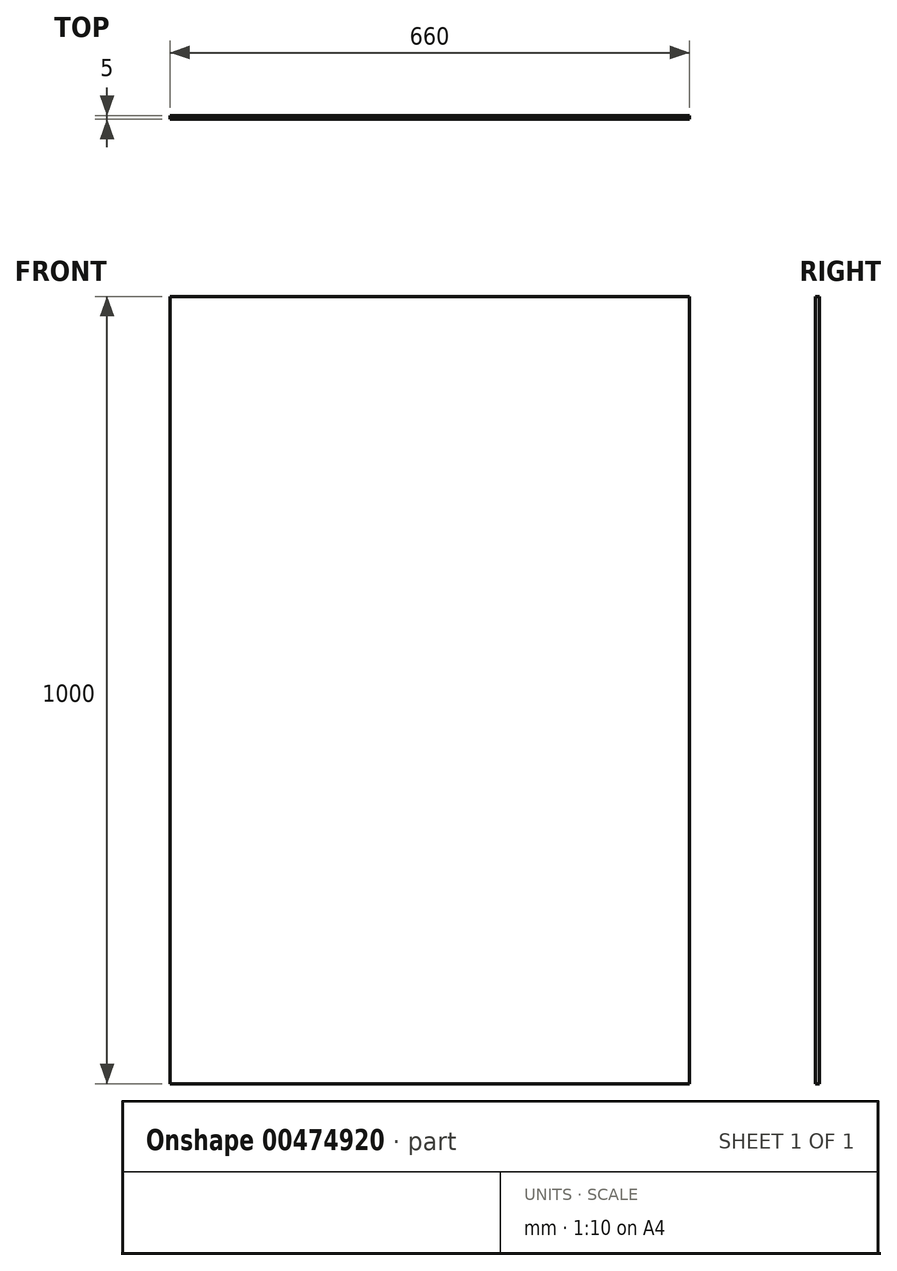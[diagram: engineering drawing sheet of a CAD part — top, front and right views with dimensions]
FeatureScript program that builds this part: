
annotation { "Feature Type Name" : "Feature", "Feature Type Description" : "" }
export const myFeature = defineFeature(function(context is Context, id is Id, definition is map)
    precondition{}
    {
        {
            var Q0;
            Q0=qCreatedBy(makeId("Front.planeOp"),FACE);
            var sketch = newSketch(context, id + "F0", { "sketchPlane" : qUnion([Q0])});
            skLineSegment(sketch, "E0.bottom", {"start": v(-279.26, 770.08) * mm, "end": v(380.74, 770.08) * mm});
            skLineSegment(sketch, "E0.top", {"start": v(-279.26, -229.92) * mm, "end": v(380.74, -229.92) * mm});
            skLineSegment(sketch, "E0.left", {"start": v(-279.26, 770.08) * mm, "end": v(-279.26, -229.92) * mm});
            skLineSegment(sketch, "E0.right", {"start": v(380.74, 770.08) * mm, "end": v(380.74, -229.92) * mm});
            skPoint(sketch, "E1.endSnap0", {"position": v(50.74, 770.08) * mm});
            skSolve(sketch);
        }
        {
            var Q0;
            Q0=makeQuery(id+"F0.imprint","IMPRINT",FACE,{"disambiguationData":[TD([[makeQuery(id+"F0.imprint","IMPRINT",EDGE,{"derivedFrom":sQuery(id+"F0.wireOp",EDGE,"E0.bottom")}),-1.0]])]});
            extrude(context, id + "F1", {"entities" : qUnion([Q0]), "depth" : 5 * mm});
        }
    });
